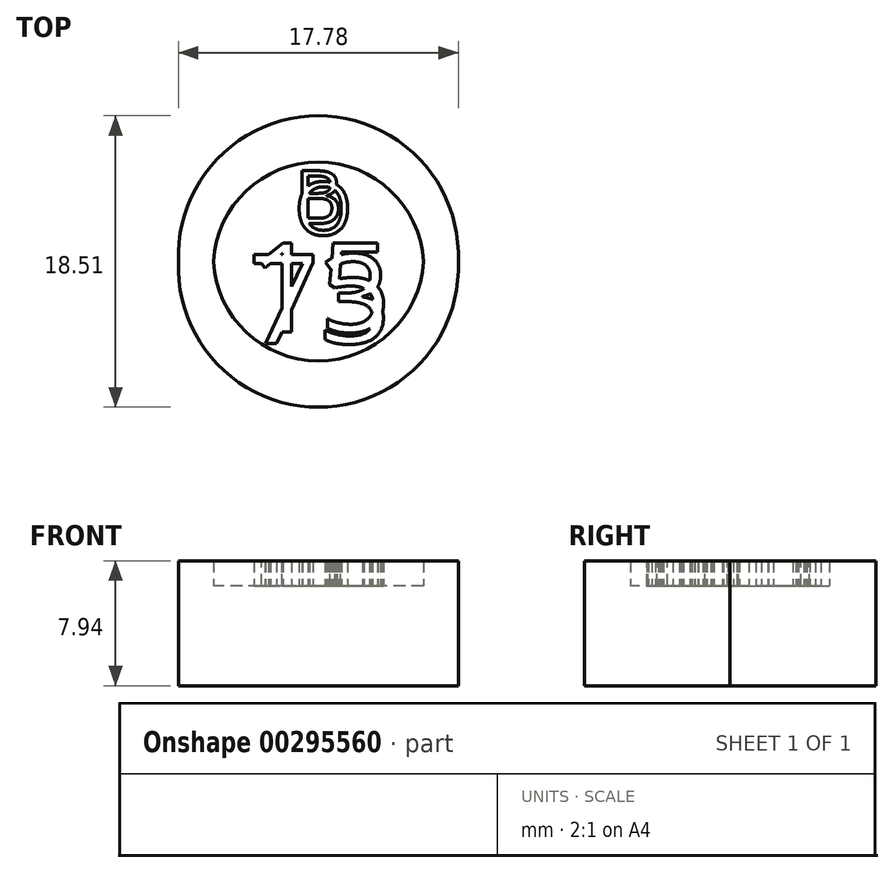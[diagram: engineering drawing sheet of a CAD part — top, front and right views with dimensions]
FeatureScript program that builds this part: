
annotation { "Feature Type Name" : "Feature", "Feature Type Description" : "" }
export const myFeature = defineFeature(function(context is Context, id is Id, definition is map)
    precondition{}
    {
        {
            var Q0;
            Q0=qCreatedBy(makeId("Top.planeOp"),FACE);
            var sketch = newSketch(context, id + "F0", { "sketchPlane" : qUnion([Q0])});
            skCircle(sketch, "E0", {"center": v(0, 0) * mm, "radius": 8.9 * mm});
            skLineSegment(sketch, "E1", {"start": v(-8.65, 2.05) * mm, "end": v(8.65, 2.05) * mm, "construction": true});
            skText(sketch, "E2", { "text": "B", "fontName": "OpenSans-Regular.ttf"});
            skCircle(sketch, "E3", {"center": v(0, 0) * mm, "radius": 6.68 * mm});
            skLineSegment(sketch, "E4", {"start": v(-8.85, 0.88) * mm, "end": v(8.85, 0.88) * mm, "construction": true});
            skText(sketch, "E5", { "text": "15", "fontName": "OpenSans-Regular.ttf"});
            const initialGuessF0  = {"E2": [-0.00151, 0.00205, 1, 0, 0.00338], "E5": [-0.00446, -0.00483, 1, 0, 0.0057]};
            skSetInitialGuess(sketch, initialGuessF0);
            skSolve(sketch);
        }
        {
            var Q0;
            Q0=makeQuery(id+"F0.imprint","IMPRINT",FACE,{"disambiguationData":[TD([[makeQuery(id+"F0.imprint","IMPRINT",EDGE,{"derivedFrom":sQuery(id+"F0.wireOp",EDGE,"E0")}),1.0]])]});
            var Q1;
            Q1=makeQuery(id+"F0.imprint","IMPRINT",FACE,{"disambiguationData":[TD([[makeQuery(id+"F0.imprint","IMPRINT",EDGE,{"derivedFrom":sQuery(id+"F0.wireOp",EDGE,"E5.sketch_text.stroke-0")}),-1.0]])]});
            var Q2;
            Q2=makeQuery(id+"F0.imprint","IMPRINT",FACE,{"disambiguationData":[TD([[makeQuery(id+"F0.imprint","IMPRINT",EDGE,{"derivedFrom":sQuery(id+"F0.wireOp",EDGE,"E5.sketch_text.stroke-9")}),-1.0]])]});
            var Q3;
            Q3=makeQuery(id+"F0.imprint","IMPRINT",FACE,{"disambiguationData":[TD([[makeQuery(id+"F0.imprint","IMPRINT",EDGE,{"derivedFrom":sQuery(id+"F0.wireOp",EDGE,"E2.sketch_text.stroke-0")}),-1.0]])]});
            extrude(context, id + "F1", {"entities" : qUnion([Q0, Q1, Q2, Q3]), "depth" : 7.94 * mm});
        }
        {
            var Q0;
            Q0=makeQuery(id+"F0.imprint","IMPRINT",FACE,{"disambiguationData":[TD([[makeQuery(id+"F0.imprint","IMPRINT",EDGE,{"derivedFrom":sQuery(id+"F0.wireOp",EDGE,"E2.sketch_text.stroke-0")}),1.0]])]});
            var Q1;
            Q1=makeQuery(id+"F0.imprint","IMPRINT",FACE,{"disambiguationData":[TD([[makeQuery(id+"F0.imprint","IMPRINT",EDGE,{"derivedFrom":sQuery(id+"F0.wireOp",EDGE,"E2.sketch_text.stroke-18")}),1.0]])]});
            var Q2;
            Q2=makeQuery(id+"F0.imprint","IMPRINT",FACE,{"disambiguationData":[TD([[makeQuery(id+"F0.imprint","IMPRINT",EDGE,{"derivedFrom":sQuery(id+"F0.wireOp",EDGE,"E2.sketch_text.stroke-11")}),1.0]])]});
            extrude(context, id + "F2", {"entities" : qUnion([Q0, Q1, Q2]), "operationType" : NewBodyOperationType.ADD, "depth" : 6.35 * mm});
        }
        {
            var Q0;
            Q0=qCreatedBy(makeId("Top.planeOp"),FACE);
            var sketch = newSketch(context, id + "F3", { "sketchPlane" : qUnion([Q0])});
            skCircle(sketch, "E6", {"center": v(0, -0.73) * mm, "radius": 8.9 * mm});
            skLineSegment(sketch, "E7", {"start": v(-8.65, 1.32) * mm, "end": v(8.65, 1.32) * mm, "construction": true});
            skText(sketch, "E8", { "text": "O", "fontName": "OpenSans-Regular.ttf"});
            skCircle(sketch, "E9", {"center": v(0, -0.73) * mm, "radius": 6.68 * mm});
            skLineSegment(sketch, "E10", {"start": v(-8.85, 0.15) * mm, "end": v(8.85, 0.15) * mm, "construction": true});
            skText(sketch, "E11", { "text": "73", "fontName": "OpenSans-Regular.ttf"});
            const initialGuessF3  = {"E8": [-0.00151, 0.00132, 1, 0, 0.00338], "E11": [-0.00446, -0.00556, 1, 0, 0.0057]};
            skSetInitialGuess(sketch, initialGuessF3);
            skSolve(sketch);
        }
        {
            var Q0;
            Q0=makeQuery(id+"F3.imprint","IMPRINT",FACE,{"disambiguationData":[TD([[makeQuery(id+"F3.imprint","IMPRINT",EDGE,{"derivedFrom":sQuery(id+"F3.wireOp",EDGE,"E8.sketch_text.stroke-8")}),1.0]])]});
            var Q1;
            Q1=makeQuery(id+"F3.imprint","IMPRINT",FACE,{"disambiguationData":[TD([[makeQuery(id+"F3.imprint","IMPRINT",EDGE,{"derivedFrom":sQuery(id+"F3.wireOp",EDGE,"E8.sketch_text.stroke-0")}),1.0]])]});
            extrude(context, id + "F4", {"entities" : qUnion([Q0, Q1]), "depth" : 6.35 * mm});
        }
        {
            var Q0;
            Q0=makeQuery(id+"F3.imprint","IMPRINT",FACE,{"disambiguationData":[TD([[makeQuery(id+"F3.imprint","IMPRINT",EDGE,{"derivedFrom":sQuery(id+"F3.wireOp",EDGE,"E6")}),1.0]])]});
            var Q1;
            Q1=makeQuery(id+"F3.imprint","IMPRINT",FACE,{"disambiguationData":[TD([[makeQuery(id+"F3.imprint","IMPRINT",EDGE,{"derivedFrom":sQuery(id+"F3.wireOp",EDGE,"E11.sketch_text.stroke-0")}),-1.0]])]});
            var Q2;
            Q2=makeQuery(id+"F3.imprint","IMPRINT",FACE,{"disambiguationData":[TD([[makeQuery(id+"F3.imprint","IMPRINT",EDGE,{"derivedFrom":sQuery(id+"F3.wireOp",EDGE,"E11.sketch_text.stroke-7")}),-1.0]])]});
            var Q3;
            Q3=makeQuery(id+"F3.imprint","IMPRINT",FACE,{"disambiguationData":[TD([[makeQuery(id+"F3.imprint","IMPRINT",EDGE,{"derivedFrom":sQuery(id+"F3.wireOp",EDGE,"E8.sketch_text.stroke-0")}),-1.0]])]});
            extrude(context, id + "F5", {"entities" : qUnion([Q0, Q1, Q2, Q3]), "operationType" : NewBodyOperationType.ADD, "depth" : 7.94 * mm});
        }
    });
